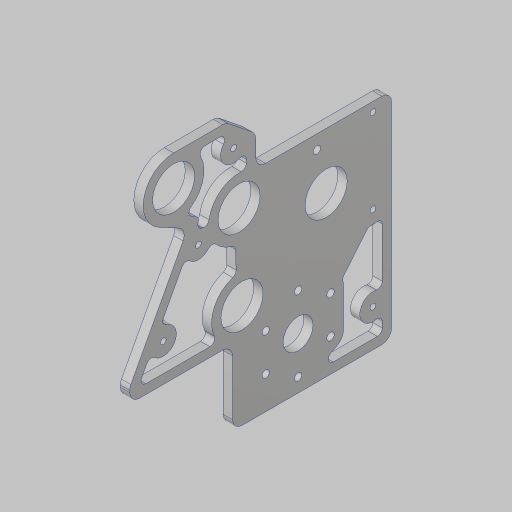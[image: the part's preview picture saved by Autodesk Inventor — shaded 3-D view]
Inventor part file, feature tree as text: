
AUTODESK INVENTOR PART (.ipt)
format: ipt  version: 2023.5 (Build 275446000, 446)  size: 428,032 bytes
history: native  units: in
note: dims shown in document units (in); Inventor stores cm internally (conversion verified against a paired STEP export)
features: sketch x6, extrude x4, hole x3, fillet x2, projected_geometry x2
ambient origin geometry x8: Origin, YZ Plane, XZ Plane, XY Plane, X Axis, Y Axis, Z Axis, Center Point
bodies: Solid1 (feature_tree)
feature tree (17):
  sketch  "Sketch1"  dims[d0=1.0in d1=12.0in]
  sketch  "Sketch2"  dims[d2=0.1924in d3=0.5in]
  extrude  "Extrusion1"  Depth=12.0in
  hole  "Hole1"  [1 undecoded]
  sketch  "Sketch3"  dims[d4=0.5in d5=0.5in]
  extrude  "Extrusion2"  Depth=0.5in
  hole  "Hole2"  [1 undecoded]
  extrude  "Extrusion3"  Depth=2.0in
  fillet  "Fillet1"  Radius=2.0in
  fillet  "Fillet2"  Radius=1.0in
  extrude  "Extrusion4"  Depth=0.8108in
  hole  "Hole3"  [1 undecoded]
  sketch  "Sketch4"  dims[d6=1.0in d7=11.067in]
  sketch  "Sketch5"  dims[d8=0.176in d9=1.176in d10=2.0in d11=1.0in]
  sketch  "Sketch6"  dims[d12=2.0in d13=1.0in d14=20.0in d15=3.572in d16=1.125in d17=0.441in d18=2.4in d19=1.375in d20=1.5in d21=0.5in d22=3.6in d23=1.0in d24=3.6in d25=1.0in d26=3.4in d27=3.342in d28=1.114in d29=5.9982in d30=1.5924in d31=7.8297in d32=1.5in d33=2.0in d34=1.125in d35=0.25in d37=0.5in d38=2.0in d39=4.0in d40=5.5in d41=1.0in d42=7.0in d43=7.5in d44=0.25in d45=0.0in d46=0.8in d47=0.5in d48=1.0in d49=4.0in d50=1.0in d51=4.5in d52=0.25in d53=0.25in d54=0.25in d55=2.0in d56=2.3622in d58=360.0deg d60=0.201in d61=0.75in d62=0.385in d63=0.25in d64=0.5635in d65=1.0in d66=0.8108in d67=0.25in d68=0.25in d69=0.0in d70=0.0in d71=0.156in d72=0.38in d73=0.375in d74=0.25in d75=0.5635in d76=1.0in d77=0.8108in d78=0.25in d79=0.25in d80=0.25in d81=0.125in d82=0.125in d83=0.125in d84=0.125in d85=0.125in d86=0.0in d87=0.0in d88=0.13in d89=0.26in d90=0.6in d91=1.125in d92=1.75in d93=1.5in d94=0.0in d95=0.0in d96=0.375in d97=2.0in d98=0.201in d99=0.75in d100=0.385in d101=0.25in d102=0.5635in d103=1.0in d104=0.8108in]
  projected_geometry  "Project Cut Edges1"
  projected_geometry  "Project Cut Edges2"
note: 3 required parameter values undecoded (feature->parameter linkage not recoverable at this tier; creation-order binding heuristic only, values carry confidence <= 0.55)
